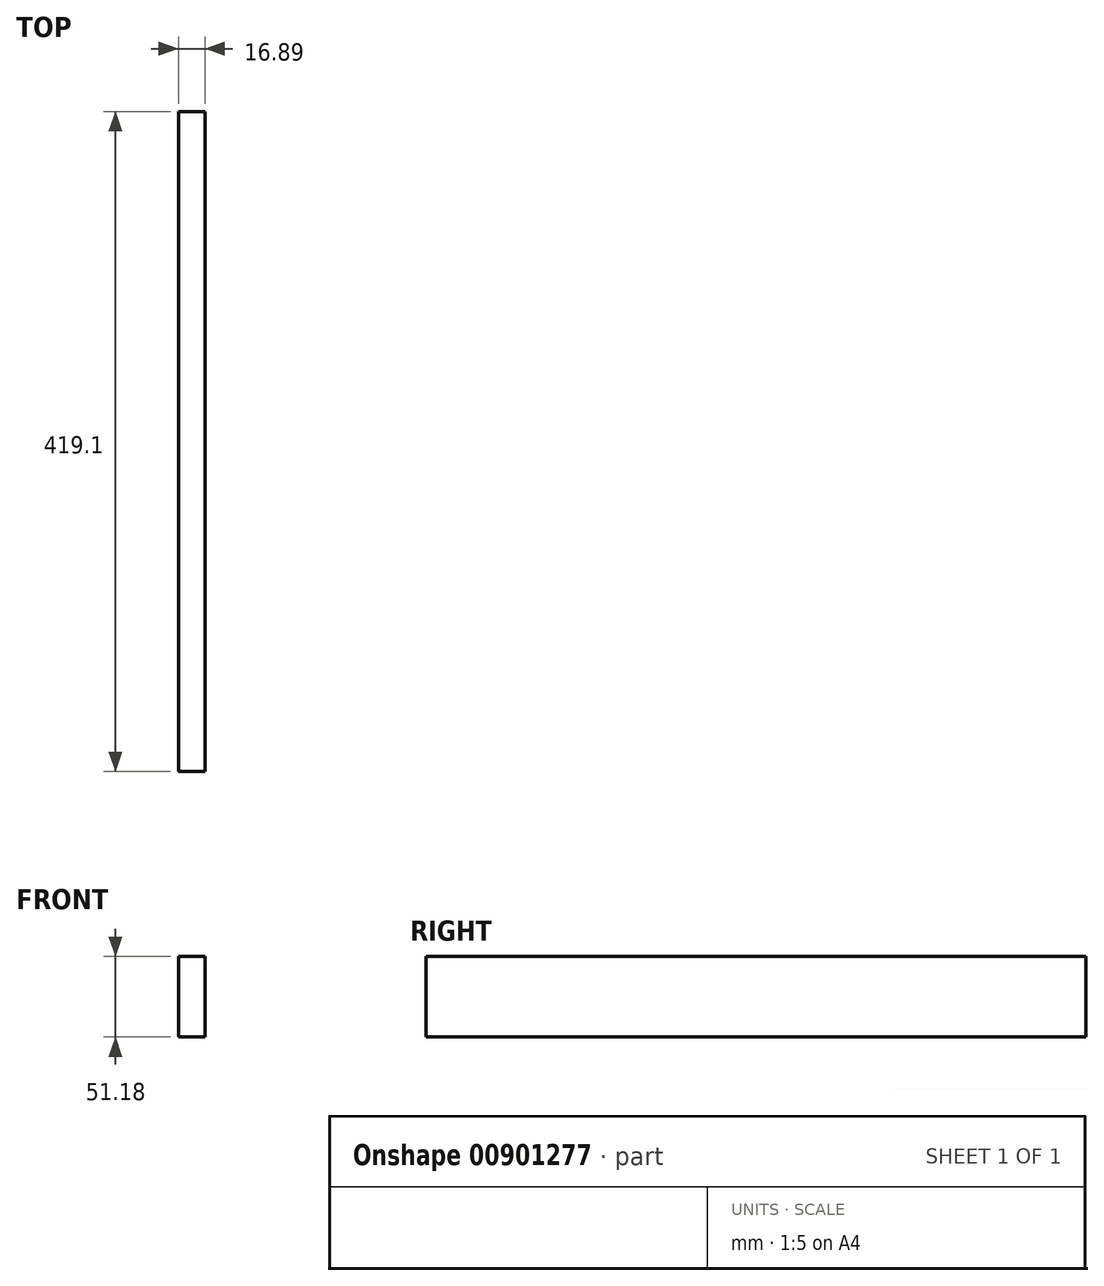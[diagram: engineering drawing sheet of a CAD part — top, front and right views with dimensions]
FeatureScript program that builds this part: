
annotation { "Feature Type Name" : "Feature", "Feature Type Description" : "" }
export const myFeature = defineFeature(function(context is Context, id is Id, definition is map)
    precondition{}
    {
        {
            var Q0;
            Q0=qCreatedBy(makeId("Right.planeOp"),FACE);
            var sketch = newSketch(context, id + "F0", { "sketchPlane" : qUnion([Q0])});
            skLineSegment(sketch, "E0.bottom", {"start": v(0, 0) * mm, "end": v(419.1, 0) * mm});
            skLineSegment(sketch, "E0.top", {"start": v(0, 51.18) * mm, "end": v(419.1, 51.18) * mm});
            skLineSegment(sketch, "E0.left", {"start": v(0, 0) * mm, "end": v(0, 51.18) * mm});
            skLineSegment(sketch, "E0.right", {"start": v(419.1, 0) * mm, "end": v(419.1, 51.18) * mm});
            skSolve(sketch);
        }
        {
            var Q0;
            Q0=qSketchRegion(id+"F0",true);
            extrude(context, id + "F1", {"entities" : qUnion([Q0]), "depth" : 16.9 * mm, "offsetDistance" : 25.4 * mm});
        }
    });
